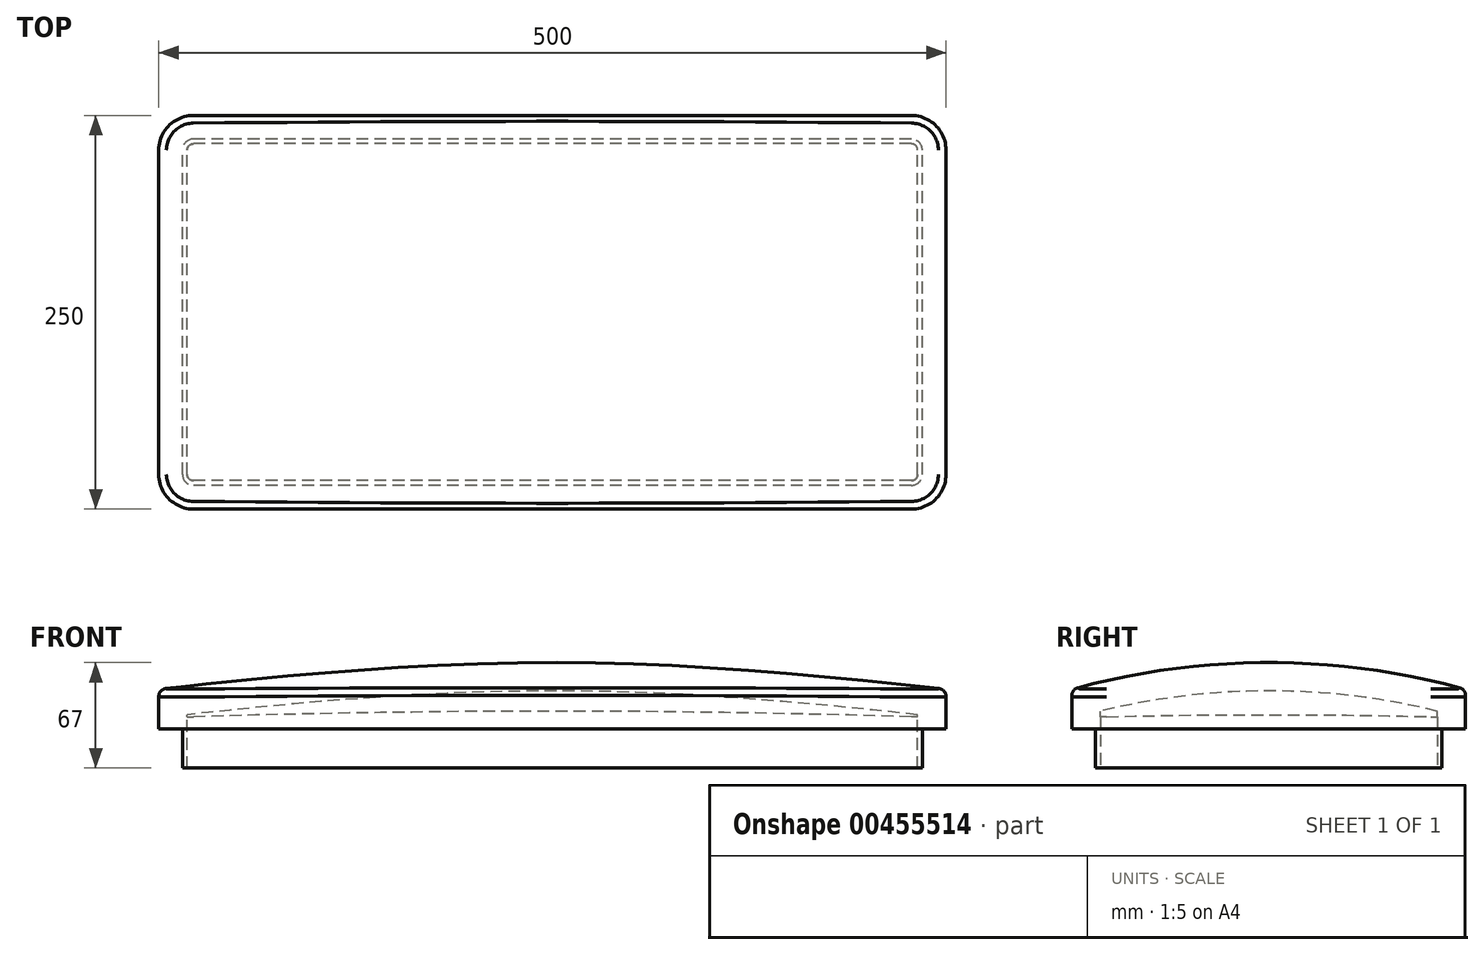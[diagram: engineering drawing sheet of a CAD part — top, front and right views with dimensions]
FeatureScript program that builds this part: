
annotation { "Feature Type Name" : "Feature", "Feature Type Description" : "" }
export const myFeature = defineFeature(function(context is Context, id is Id, definition is map)
    precondition{}
    {
        {
            var Q0;
            Q0=qCreatedBy(makeId("Top.planeOp"),FACE);
            var sketch = newSketch(context, id + "F0", { "sketchPlane" : qUnion([Q0])});
            skLineSegment(sketch, "E0.bottom", {"start": v(250, -125) * mm, "end": v(-250, -125) * mm});
            skLineSegment(sketch, "E0.top", {"start": v(250, 125) * mm, "end": v(-250, 125) * mm});
            skLineSegment(sketch, "E0.left", {"start": v(250, -125) * mm, "end": v(250, 125) * mm});
            skLineSegment(sketch, "E0.right", {"start": v(-250, -125) * mm, "end": v(-250, 125) * mm});
            skPoint(sketch, "E0.middle", {"position": v(0, 0) * mm});
            skSolve(sketch);
        }
        {
            var Q0;
            Q0 = qSketchRegion(id + "F0", true);
            extrude(context, id + "F1", {"entities" : qUnion([Q0]), "depth" : 25 * mm});
        }
        {
            var Q0;
            Q0=qCreatedBy(makeId("Right.planeOp"),FACE);
            var sketch = newSketch(context, id + "F2", { "sketchPlane" : qUnion([Q0])});
            skArc(sketch, "E1", {"start": v(125, 25) * mm, "mid": v(0, 42) * mm, "end": v(-125, 25) * mm});
            skLineSegment(sketch, "E2", {"start": v(125, 25) * mm, "end": v(-125, 25) * mm, "construction": true});
            skLineSegment(sketch, "E3.0", {"start": v(-125, 25) * mm, "end": v(-125, 0) * mm});
            skLineSegment(sketch, "E3.1", {"start": v(125, 25) * mm, "end": v(125, 0) * mm});
            skLineSegment(sketch, "E3.2", {"start": v(-125, 0) * mm, "end": v(125, 0) * mm});
            skSolve(sketch);
        }
        {
            var Q0;
            Q0=qCreatedBy(makeId("Front.planeOp"),FACE);
            var sketch = newSketch(context, id + "F3", { "sketchPlane" : qUnion([Q0])});
            skFitSpline(sketch, "E4", {"points": [v(-250, 25) * mm, v(250, 25) * mm], "startDerivative": vector(608.4, 68) * mm, "endDerivative": vector(608.4, -68) * mm});
            skSolve(sketch);
        }
        {
            var Q1;
            Q1=makeQuery(id+"F1.opExtrude","SWEPT_FACE",FACE,{"disambiguationData":[OSD([sQuery(id+"F0.wireOp",EDGE,"E0.left")])]});
            var Q2;
            Q2=makeQuery(id+"F2.imprint","IMPRINT",FACE,{"disambiguationData":[TD([[makeQuery(id+"F2.imprint","IMPRINT",EDGE,{"derivedFrom":sQuery(id+"F2.wireOp",EDGE,"E1")}),1.0]])]});
            var Q3;
            Q3=makeQuery(id+"F1.opExtrude","SWEPT_FACE",FACE,{"disambiguationData":[OSD([sQuery(id+"F0.wireOp",EDGE,"E0.right")])]});
            var Q4;
            Q4=sQuery(id+"F3.wireOp",EDGE,"E4");
            loft(context, id + "F4", {"operationType" : NewBodyOperationType.ADD, "addGuides" : true, "sheetProfilesArray" : [{ "sheetProfileEntities" : qUnion([Q1]) }, { "sheetProfileEntities" : qUnion([Q2]) }, { "sheetProfileEntities" : qUnion([Q3]) }], "guidesArray" : [{ "guideEntities" : qUnion([Q4]), "guideDerivativeType" : LoftGuideDerivativeType.DEFAULT, "guideDerivativeMagnitude" : 1 }]});
        }
        {
            var Q0;
            Q0=makeQuery(id+"F1.opExtrude","SWEPT_EDGE",EDGE,{"disambiguationData":[OSD([sQuery(id+"F0.wireOp",EDGE,"E0.bottom"),sQuery(id+"F0.wireOp",EDGE,"E0.right")])]});
            var Q1;
            Q1=makeQuery(id+"F1.opExtrude","SWEPT_EDGE",EDGE,{"disambiguationData":[OSD([sQuery(id+"F0.wireOp",EDGE,"E0.bottom"),sQuery(id+"F0.wireOp",EDGE,"E0.left")])]});
            var Q2;
            Q2=makeQuery(id+"F1.opExtrude","SWEPT_EDGE",EDGE,{"disambiguationData":[OSD([sQuery(id+"F0.wireOp",EDGE,"E0.top"),sQuery(id+"F0.wireOp",EDGE,"E0.left")])]});
            var Q3;
            Q3=makeQuery(id+"F1.opExtrude","SWEPT_EDGE",EDGE,{"disambiguationData":[OSD([sQuery(id+"F0.wireOp",EDGE,"E0.top"),sQuery(id+"F0.wireOp",EDGE,"E0.right")])]});
            var Q4;
            Q4=makeQuery(id+"Fj6lcFS6ckg576c_1.opPattern","COPY",EDGE,{"derivedFrom":makeQuery(id+"F1.opExtrude","SWEPT_EDGE",EDGE,{"disambiguationData":[OSD([sQuery(id+"F0.wireOp",EDGE,"E0.top"),sQuery(id+"F0.wireOp",EDGE,"E0.right")])]}),"instanceName":"1"});
            var Q5;
            Q5=makeQuery(id+"Fj6lcFS6ckg576c_1.opPattern","COPY",EDGE,{"derivedFrom":makeQuery(id+"F1.opExtrude","SWEPT_EDGE",EDGE,{"disambiguationData":[OSD([sQuery(id+"F0.wireOp",EDGE,"E0.top"),sQuery(id+"F0.wireOp",EDGE,"E0.left")])]}),"instanceName":"1"});
            fillet(context, id + "F5", {"entities" : qUnion([Q0, Q1, Q2, Q3, Q4, Q5]), "radius" : 22 * mm, "tangentPropagation" : true, "allowEdgeOverflow" : false});
        }
        {
            var Q0;
            {var subQ0=sQuery(id+"F0.wireOp",EDGE,"E0.left");Q0=makeQuery(id+"F4.boolean.opBoolean","MERGE",EDGE,{"derivedFrom":[makeQuery(id+"F1.opExtrude","CAP_EDGE",EDGE,{"disambiguationData":[OSD([subQ0])],"isStart":false}),makeQuery(id+"F4.opLoft","MID_CAP_EDGE",EDGE,{"disambiguationData":[OSD([sQuery(id+"F0.wireOp",EDGE,"E0.bottom"),subQ0,sQuery(id+"F3.wireOp",EDGE,"E4")])],"capPos":0.0})]});}
            fillet(context, id + "F6", {"entities" : qUnion([Q0]), "radius" : 5 * mm, "tangentPropagation" : true, "allowEdgeOverflow" : false});
        }
        {
            var Q0;
            Q0=makeQuery(id+"F1.opExtrude","CAP_FACE",FACE,{"disambiguationData":[OSD([sQuery(id+"F0.wireOp",EDGE,"E0.bottom"),sQuery(id+"F0.wireOp",EDGE,"E0.top"),sQuery(id+"F0.wireOp",EDGE,"E0.left"),sQuery(id+"F0.wireOp",EDGE,"E0.right")])],"isStart":true});
            shell(context, id + "F7", {"entities" : qUnion([Q0]), "thickness" : 18 * mm});
        }
        {
            var Q0;
            {var subQ0=makeQuery(id+"FCfvGYRV0cBQWJA_1.splitOp","SPLIT",FACE,{"derivedFrom":makeQuery(id+"F1.opExtrude","CAP_FACE",FACE,{"disambiguationData":[OSD([sQuery(id+"F0.wireOp",EDGE,"E0.bottom"),sQuery(id+"F0.wireOp",EDGE,"E0.top"),sQuery(id+"F0.wireOp",EDGE,"E0.left"),sQuery(id+"F0.wireOp",EDGE,"E0.right")])],"isStart":true}),"isFromBackBody":true});Q0=makeQuery(id+"Fj6lcFS6ckg576c_1.boolean.opBoolean","MERGE",FACE,{"derivedFrom":[subQ0,makeQuery(id+"Fj6lcFS6ckg576c_1.opPattern","COPY",FACE,{"derivedFrom":subQ0,"instanceName":"1"})]});}
            var sketch = newSketch(context, id + "F8", { "sketchPlane" : qUnion([Q0])});
            skArc(sketch, "E5.0", {"start": v(235, 103) * mm, "mid": v(232.95, 107.95) * mm, "end": v(228, 110) * mm});
            skLineSegment(sketch, "E5.1", {"start": v(235, 103) * mm, "end": v(235, -103) * mm});
            skLineSegment(sketch, "E5.2", {"start": v(228, 110) * mm, "end": v(-228, 110) * mm});
            skArc(sketch, "E5.3", {"start": v(228, -110) * mm, "mid": v(232.95, -107.95) * mm, "end": v(235, -103) * mm});
            skArc(sketch, "E5.4", {"start": v(-228, 110) * mm, "mid": v(-232.95, 107.95) * mm, "end": v(-235, 103) * mm});
            skLineSegment(sketch, "E5.5", {"start": v(-235, 103) * mm, "end": v(-235, -103) * mm});
            skArc(sketch, "E5.6", {"start": v(-235, -103) * mm, "mid": v(-232.95, -107.95) * mm, "end": v(-228, -110) * mm});
            skLineSegment(sketch, "E5.7", {"start": v(228, -110) * mm, "end": v(-228, -110) * mm});
            skSolve(sketch);
        }
        {
            var Q0;
            Q0=makeQuery(id+"F8.imprint","IMPRINT",FACE,{"disambiguationData":[TD([[makeQuery(id+"F8.imprint","IMPRINT",EDGE,{"derivedFrom":sQuery(id+"F8.wireOp",EDGE,"E5.0")}),1.0]])]});
            extrude(context, id + "F9", {"entities" : qUnion([Q0]), "operationType" : NewBodyOperationType.ADD, "depth" : 25 * mm});
        }
    });
